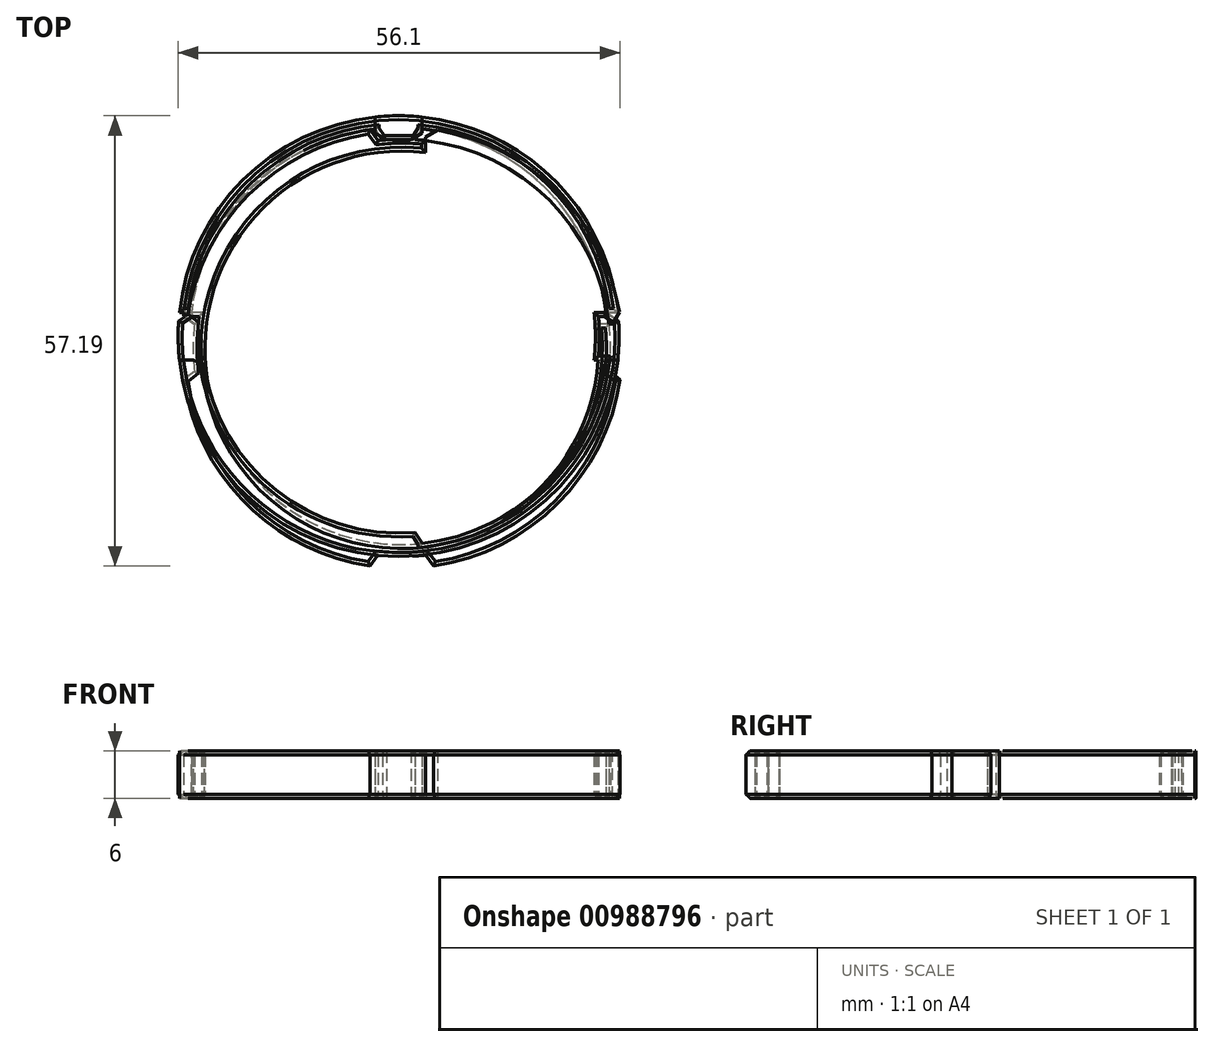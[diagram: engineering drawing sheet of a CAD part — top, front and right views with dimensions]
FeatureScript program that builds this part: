
annotation { "Feature Type Name" : "Feature", "Feature Type Description" : "" }
export const myFeature = defineFeature(function(context is Context, id is Id, definition is map)
    precondition{}
    {
        {
            var Q0;
            Q0=qCreatedBy(makeId("Top.planeOp"),FACE);
            var sketch = newSketch(context, id + "F0", { "sketchPlane" : qUnion([Q0])});
            skCircle(sketch, "E0", {"center": v(0, 0) * mm, "radius": 28 * mm});
            skCircle(sketch, "E1", {"center": v(0, 0) * mm, "radius": 25 * mm});
            skLineSegment(sketch, "E2.bottom", {"start": v(53.13, -3) * mm, "end": v(-53.13, -3) * mm});
            skLineSegment(sketch, "E2.top", {"start": v(53.13, 3) * mm, "end": v(-53.13, 3) * mm});
            skLineSegment(sketch, "E2.left", {"start": v(53.13, -3) * mm, "end": v(53.13, 3) * mm});
            skLineSegment(sketch, "E2.right", {"start": v(-53.13, -3) * mm, "end": v(-53.13, 3) * mm});
            skCircle(sketch, "E3", {"center": v(0, 0) * mm, "radius": 26.5 * mm});
            skLineSegment(sketch, "E4.bottom", {"start": v(3, -37.45) * mm, "end": v(-3, -37.45) * mm});
            skLineSegment(sketch, "E4.top", {"start": v(3, 37.45) * mm, "end": v(-3, 37.45) * mm});
            skLineSegment(sketch, "E4.left", {"start": v(3, -37.45) * mm, "end": v(3, 37.45) * mm});
            skLineSegment(sketch, "E4.right", {"start": v(-3, -37.45) * mm, "end": v(-3, 37.45) * mm});
            skSolve(sketch);
        }
        {
            var Q0;
            {var subQ0=sQuery(id+"F0.wireOp",EDGE,"E2.bottom");var subQ1=sQuery(id+"F0.wireOp",EDGE,"E1");var subQ2=makeQuery(id+"F0.imprint","INTERSECT",VERTEX,{"disambiguationData":[OD(0.0)],"derivedFrom":[subQ1,subQ0]});Q0=makeQuery(id+"F0.imprint","IMPRINT",FACE,{"disambiguationData":[TD([[makeQuery(id+"F0.imprint","IMPRINT",EDGE,{"disambiguationData":[TD([[subQ2,-1.0]])],"derivedFrom":subQ1}),-1.0]])]});}
            var Q1;
            {var subQ0=sQuery(id+"F0.wireOp",EDGE,"E2.top");var subQ1=sQuery(id+"F0.wireOp",EDGE,"E1");var subQ2=makeQuery(id+"F0.imprint","INTERSECT",VERTEX,{"disambiguationData":[OD(0.0)],"derivedFrom":[subQ1,subQ0]});Q1=makeQuery(id+"F0.imprint","IMPRINT",FACE,{"disambiguationData":[TD([[makeQuery(id+"F0.imprint","IMPRINT",EDGE,{"disambiguationData":[TD([[subQ2,1.0]])],"derivedFrom":subQ1}),-1.0]])]});}
            var Q2;
            {var subQ0=sQuery(id+"F0.wireOp",EDGE,"E2.bottom");var subQ1=sQuery(id+"F0.wireOp",EDGE,"E0");var subQ2=makeQuery(id+"F0.imprint","INTERSECT",VERTEX,{"disambiguationData":[OD(0.0)],"derivedFrom":[subQ1,subQ0]});Q2=makeQuery(id+"F0.imprint","IMPRINT",FACE,{"disambiguationData":[TD([[makeQuery(id+"F0.imprint","IMPRINT",EDGE,{"disambiguationData":[TD([[subQ2,-1.0]])],"derivedFrom":subQ1}),1.0]])]});}
            var Q3;
            {var subQ0=sQuery(id+"F0.wireOp",EDGE,"E2.top");var subQ1=sQuery(id+"F0.wireOp",EDGE,"E0");var subQ2=makeQuery(id+"F0.imprint","INTERSECT",VERTEX,{"disambiguationData":[OD(0.0)],"derivedFrom":[subQ1,subQ0]});Q3=makeQuery(id+"F0.imprint","IMPRINT",FACE,{"disambiguationData":[TD([[makeQuery(id+"F0.imprint","IMPRINT",EDGE,{"disambiguationData":[TD([[subQ2,-1.0]])],"derivedFrom":subQ1}),1.0]])]});}
            var Q4;
            {var subQ0=sQuery(id+"F0.wireOp",EDGE,"E2.top");var subQ1=sQuery(id+"F0.wireOp",EDGE,"E0");var subQ2=makeQuery(id+"F0.imprint","INTERSECT",VERTEX,{"disambiguationData":[OD(1.0)],"derivedFrom":[subQ1,subQ0]});Q4=makeQuery(id+"F0.imprint","IMPRINT",FACE,{"disambiguationData":[TD([[makeQuery(id+"F0.imprint","IMPRINT",EDGE,{"disambiguationData":[TD([[subQ2,1.0]])],"derivedFrom":subQ1}),1.0]])]});}
            var Q5;
            {var subQ0=sQuery(id+"F0.wireOp",EDGE,"E4.left");var subQ1=sQuery(id+"F0.wireOp",EDGE,"E0");var subQ2=makeQuery(id+"F0.imprint","INTERSECT",VERTEX,{"disambiguationData":[OD(0.0)],"derivedFrom":[subQ1,subQ0]});Q5=makeQuery(id+"F0.imprint","IMPRINT",FACE,{"disambiguationData":[TD([[makeQuery(id+"F0.imprint","IMPRINT",EDGE,{"disambiguationData":[TD([[subQ2,-1.0]])],"derivedFrom":subQ1}),1.0]])]});}
            var Q6;
            {var subQ0=sQuery(id+"F0.wireOp",EDGE,"E4.left");var subQ1=sQuery(id+"F0.wireOp",EDGE,"E1");var subQ2=makeQuery(id+"F0.imprint","INTERSECT",VERTEX,{"disambiguationData":[OD(0.0)],"derivedFrom":[subQ1,subQ0]});Q6=makeQuery(id+"F0.imprint","IMPRINT",FACE,{"disambiguationData":[TD([[makeQuery(id+"F0.imprint","IMPRINT",EDGE,{"disambiguationData":[TD([[subQ2,1.0]])],"derivedFrom":subQ1}),-1.0]])]});}
            var Q7;
            {var subQ0=sQuery(id+"F0.wireOp",EDGE,"E4.left");var subQ1=sQuery(id+"F0.wireOp",EDGE,"E1");var subQ2=makeQuery(id+"F0.imprint","INTERSECT",VERTEX,{"disambiguationData":[OD(1.0)],"derivedFrom":[subQ1,subQ0]});Q7=makeQuery(id+"F0.imprint","IMPRINT",FACE,{"disambiguationData":[TD([[makeQuery(id+"F0.imprint","IMPRINT",EDGE,{"disambiguationData":[TD([[subQ2,-1.0]])],"derivedFrom":subQ1}),-1.0]])]});}
            var Q8;
            {var subQ0=sQuery(id+"F0.wireOp",EDGE,"E4.right");var subQ1=sQuery(id+"F0.wireOp",EDGE,"E1");var subQ2=makeQuery(id+"F0.imprint","INTERSECT",VERTEX,{"disambiguationData":[OD(0.0)],"derivedFrom":[subQ1,subQ0]});Q8=makeQuery(id+"F0.imprint","IMPRINT",FACE,{"disambiguationData":[TD([[makeQuery(id+"F0.imprint","IMPRINT",EDGE,{"disambiguationData":[TD([[subQ2,-1.0]])],"derivedFrom":subQ1}),-1.0]])]});}
            var Q9;
            {var subQ0=sQuery(id+"F0.wireOp",EDGE,"E4.left");var subQ1=sQuery(id+"F0.wireOp",EDGE,"E0");var subQ2=makeQuery(id+"F0.imprint","INTERSECT",VERTEX,{"disambiguationData":[OD(1.0)],"derivedFrom":[subQ1,subQ0]});Q9=makeQuery(id+"F0.imprint","IMPRINT",FACE,{"disambiguationData":[TD([[makeQuery(id+"F0.imprint","IMPRINT",EDGE,{"disambiguationData":[TD([[subQ2,-1.0]])],"derivedFrom":subQ1}),1.0]])]});}
            var Q10;
            {var subQ0=sQuery(id+"F0.wireOp",EDGE,"E4.right");var subQ1=sQuery(id+"F0.wireOp",EDGE,"E0");var subQ2=makeQuery(id+"F0.imprint","INTERSECT",VERTEX,{"disambiguationData":[OD(1.0)],"derivedFrom":[subQ1,subQ0]});Q10=makeQuery(id+"F0.imprint","IMPRINT",FACE,{"disambiguationData":[TD([[makeQuery(id+"F0.imprint","IMPRINT",EDGE,{"disambiguationData":[TD([[subQ2,-1.0]])],"derivedFrom":subQ1}),1.0]])]});}
            var Q11;
            {var subQ0=sQuery(id+"F0.wireOp",EDGE,"E2.top");var subQ1=sQuery(id+"F0.wireOp",EDGE,"E1");var subQ2=makeQuery(id+"F0.imprint","INTERSECT",VERTEX,{"disambiguationData":[OD(1.0)],"derivedFrom":[subQ1,subQ0]});Q11=makeQuery(id+"F0.imprint","IMPRINT",FACE,{"disambiguationData":[TD([[makeQuery(id+"F0.imprint","IMPRINT",EDGE,{"disambiguationData":[TD([[subQ2,-1.0]])],"derivedFrom":subQ1}),-1.0]])]});}
            extrude(context, id + "F1", {"entities" : qUnion([Q0, Q1, Q2, Q3, Q4, Q5, Q6, Q7, Q8, Q9, Q10, Q11]), "depth" : 6 * mm, "offsetDistance" : 25 * mm});
        }
        {
            var Q0;
            {var subQ0=sQuery(id+"F0.wireOp",EDGE,"E4.right");var subQ1=sQuery(id+"F0.wireOp",EDGE,"E1");Q0=makeQuery(id+"F1.opExtrude","SWEPT_EDGE",EDGE,{"disambiguationData":[OSD([subQ1,subQ0]),TDD([makeQuery(id+"F0.imprint","INTERSECT",VERTEX,{"disambiguationData":[OD(0.0)],"derivedFrom":[subQ1,subQ0]})])]});}
            var Q1;
            {var subQ0=sQuery(id+"F0.wireOp",EDGE,"E4.left");var subQ1=sQuery(id+"F0.wireOp",EDGE,"E1");Q1=makeQuery(id+"F1.opExtrude","SWEPT_EDGE",EDGE,{"disambiguationData":[OSD([subQ1,subQ0]),TDD([makeQuery(id+"F0.imprint","INTERSECT",VERTEX,{"disambiguationData":[OD(1.0)],"derivedFrom":[subQ1,subQ0]})])]});}
            chamfer(context, id + "F2", {"entities" : qUnion([Q0, Q1]), "chamferType" : ChamferType.TWO_OFFSETS, "width1" : 1.5 * mm, "oppositeDirection" : false, "width2" : 1 * mm, "tangentPropagation" : true});
        }
        {
            var Q0;
            {var subQ0=sQuery(id+"F0.wireOp",EDGE,"E4.left");var subQ1=sQuery(id+"F0.wireOp",EDGE,"E1");Q0=makeQuery(id+"F1.opExtrude","SWEPT_EDGE",EDGE,{"disambiguationData":[OSD([subQ1,subQ0]),TDD([makeQuery(id+"F0.imprint","INTERSECT",VERTEX,{"disambiguationData":[OD(0.0)],"derivedFrom":[subQ1,subQ0]})])]});}
            var Q1;
            {var subQ0=sQuery(id+"F0.wireOp",EDGE,"E4.right");var subQ1=sQuery(id+"F0.wireOp",EDGE,"E1");Q1=makeQuery(id+"F1.opExtrude","SWEPT_EDGE",EDGE,{"disambiguationData":[OSD([subQ1,subQ0]),TDD([makeQuery(id+"F0.imprint","INTERSECT",VERTEX,{"disambiguationData":[OD(1.0)],"derivedFrom":[subQ1,subQ0]})])]});}
            chamfer(context, id + "F3", {"entities" : qUnion([Q0, Q1]), "chamferType" : ChamferType.TWO_OFFSETS, "width1" : 1 * mm, "oppositeDirection" : false, "width2" : 1.5 * mm, "tangentPropagation" : true});
        }
        {
            var Q0;
            {var subQ0=sQuery(id+"F0.wireOp",EDGE,"E2.bottom");var subQ1=sQuery(id+"F0.wireOp",EDGE,"E0");Q0=makeQuery(id+"F1.opExtrude","SWEPT_EDGE",EDGE,{"disambiguationData":[OSD([subQ1,subQ0]),TDD([makeQuery(id+"F0.imprint","INTERSECT",VERTEX,{"disambiguationData":[OD(1.0)],"derivedFrom":[subQ1,subQ0]})])]});}
            var Q1;
            {var subQ0=sQuery(id+"F0.wireOp",EDGE,"E2.top");var subQ1=sQuery(id+"F0.wireOp",EDGE,"E0");Q1=makeQuery(id+"F1.opExtrude","SWEPT_EDGE",EDGE,{"disambiguationData":[OSD([subQ1,subQ0]),TDD([makeQuery(id+"F0.imprint","INTERSECT",VERTEX,{"disambiguationData":[OD(1.0)],"derivedFrom":[subQ1,subQ0]})])]});}
            chamfer(context, id + "F4", {"entities" : qUnion([Q0, Q1]), "chamferType" : ChamferType.TWO_OFFSETS, "width1" : 1 * mm, "oppositeDirection" : true, "width2" : 1.5 * mm, "tangentPropagation" : true});
        }
        {
            var Q0;
            {var subQ0=sQuery(id+"F0.wireOp",EDGE,"E2.bottom");var subQ1=sQuery(id+"F0.wireOp",EDGE,"E0");Q0=makeQuery(id+"F1.opExtrude","SWEPT_EDGE",EDGE,{"disambiguationData":[OSD([subQ1,subQ0]),TDD([makeQuery(id+"F0.imprint","INTERSECT",VERTEX,{"disambiguationData":[OD(0.0)],"derivedFrom":[subQ1,subQ0]})])]});}
            var Q1;
            {var subQ0=sQuery(id+"F0.wireOp",EDGE,"E2.top");var subQ1=sQuery(id+"F0.wireOp",EDGE,"E0");Q1=makeQuery(id+"F1.opExtrude","SWEPT_EDGE",EDGE,{"disambiguationData":[OSD([subQ1,subQ0]),TDD([makeQuery(id+"F0.imprint","INTERSECT",VERTEX,{"disambiguationData":[OD(0.0)],"derivedFrom":[subQ1,subQ0]})])]});}
            chamfer(context, id + "F5", {"entities" : qUnion([Q0, Q1]), "chamferType" : ChamferType.TWO_OFFSETS, "width1" : 1 * mm, "oppositeDirection" : false, "width2" : 1.5 * mm, "tangentPropagation" : true});
        }
        {
            var Q0;
            Q0=makeQuery(id+"F1.opExtrude","CAP_FACE",FACE,{"disambiguationData":[OSD([sQuery(id+"F0.wireOp",EDGE,"E0"),sQuery(id+"F0.wireOp",EDGE,"E1"),sQuery(id+"F0.wireOp",EDGE,"E2.bottom"),sQuery(id+"F0.wireOp",EDGE,"E2.top"),sQuery(id+"F0.wireOp",EDGE,"E3"),sQuery(id+"F0.wireOp",EDGE,"E4.left"),sQuery(id+"F0.wireOp",EDGE,"E4.right")])],"isStart":false});
            var Q1;
            Q1=makeQuery(id+"F1.opExtrude","CAP_FACE",FACE,{"disambiguationData":[OSD([sQuery(id+"F0.wireOp",EDGE,"E0"),sQuery(id+"F0.wireOp",EDGE,"E1"),sQuery(id+"F0.wireOp",EDGE,"E2.bottom"),sQuery(id+"F0.wireOp",EDGE,"E2.top"),sQuery(id+"F0.wireOp",EDGE,"E3"),sQuery(id+"F0.wireOp",EDGE,"E4.left"),sQuery(id+"F0.wireOp",EDGE,"E4.right")])],"isStart":true});
            chamfer(context, id + "F6", {"entities" : qUnion([Q0, Q1]), "width" : 0.5 * mm, "tangentPropagation" : true});
        }
        {
            var Q0;
            Q0=qCreatedBy(makeId("Top.planeOp"),FACE);
            var sketch = newSketch(context, id + "F7", { "sketchPlane" : qUnion([Q0])});
            skCircle(sketch, "E5", {"center": v(0.4, -1.48) * mm, "radius": 28 * mm});
            skCircle(sketch, "E6", {"center": v(0.4, -1.48) * mm, "radius": 25 * mm});
            skLineSegment(sketch, "E7.bottom", {"start": v(53.53, -4.48) * mm, "end": v(-52.73, -4.48) * mm});
            skLineSegment(sketch, "E7.top", {"start": v(53.53, 1.52) * mm, "end": v(-52.73, 1.52) * mm});
            skLineSegment(sketch, "E7.left", {"start": v(53.53, -4.48) * mm, "end": v(53.53, 1.52) * mm});
            skLineSegment(sketch, "E7.right", {"start": v(-52.73, -4.48) * mm, "end": v(-52.73, 1.52) * mm});
            skCircle(sketch, "E8", {"center": v(0.4, -1.48) * mm, "radius": 26.5 * mm});
            skLineSegment(sketch, "E9.bottom", {"start": v(-2.6, -40.61) * mm, "end": v(3.4, -40.61) * mm});
            skLineSegment(sketch, "E9.top", {"start": v(-2.6, 37.65) * mm, "end": v(3.4, 37.65) * mm});
            skLineSegment(sketch, "E9.left", {"start": v(-2.6, -40.61) * mm, "end": v(-2.6, 37.65) * mm});
            skLineSegment(sketch, "E9.right", {"start": v(3.4, -40.61) * mm, "end": v(3.4, 37.65) * mm});
            skSolve(sketch);
        }
        {
            var Q0;
            {var subQ0=sQuery(id+"F7.wireOp",EDGE,"E9.right");var subQ1=sQuery(id+"F7.wireOp",EDGE,"E6");var subQ2=makeQuery(id+"F7.imprint","INTERSECT",VERTEX,{"disambiguationData":[OD(0.0)],"derivedFrom":[subQ1,subQ0]});Q0=makeQuery(id+"F7.imprint","IMPRINT",FACE,{"disambiguationData":[TD([[makeQuery(id+"F7.imprint","IMPRINT",EDGE,{"disambiguationData":[TD([[subQ2,-1.0]])],"derivedFrom":subQ1}),-1.0]])]});}
            var Q1;
            {var subQ0=sQuery(id+"F7.wireOp",EDGE,"E9.left");var subQ1=sQuery(id+"F7.wireOp",EDGE,"E6");var subQ2=makeQuery(id+"F7.imprint","INTERSECT",VERTEX,{"disambiguationData":[OD(0.0)],"derivedFrom":[subQ1,subQ0]});Q1=makeQuery(id+"F7.imprint","IMPRINT",FACE,{"disambiguationData":[TD([[makeQuery(id+"F7.imprint","IMPRINT",EDGE,{"disambiguationData":[TD([[subQ2,-1.0]])],"derivedFrom":subQ1}),-1.0]])]});}
            var Q2;
            {var subQ0=sQuery(id+"F7.wireOp",EDGE,"E9.left");var subQ1=sQuery(id+"F7.wireOp",EDGE,"E5");var subQ2=makeQuery(id+"F7.imprint","INTERSECT",VERTEX,{"disambiguationData":[OD(0.0)],"derivedFrom":[subQ1,subQ0]});Q2=makeQuery(id+"F7.imprint","IMPRINT",FACE,{"disambiguationData":[TD([[makeQuery(id+"F7.imprint","IMPRINT",EDGE,{"disambiguationData":[TD([[subQ2,-1.0]])],"derivedFrom":subQ1}),1.0]])]});}
            var Q3;
            {var subQ0=sQuery(id+"F7.wireOp",EDGE,"E9.right");var subQ1=sQuery(id+"F7.wireOp",EDGE,"E6");var subQ2=makeQuery(id+"F7.imprint","INTERSECT",VERTEX,{"disambiguationData":[OD(0.0)],"derivedFrom":[subQ1,subQ0]});Q3=makeQuery(id+"F7.imprint","IMPRINT",FACE,{"disambiguationData":[TD([[makeQuery(id+"F7.imprint","IMPRINT",EDGE,{"disambiguationData":[TD([[subQ2,1.0]])],"derivedFrom":subQ1}),-1.0]])]});}
            var Q4;
            {var subQ0=sQuery(id+"F7.wireOp",EDGE,"E9.right");var subQ1=sQuery(id+"F7.wireOp",EDGE,"E5");var subQ2=makeQuery(id+"F7.imprint","INTERSECT",VERTEX,{"disambiguationData":[OD(0.0)],"derivedFrom":[subQ1,subQ0]});Q4=makeQuery(id+"F7.imprint","IMPRINT",FACE,{"disambiguationData":[TD([[makeQuery(id+"F7.imprint","IMPRINT",EDGE,{"disambiguationData":[TD([[subQ2,1.0]])],"derivedFrom":subQ1}),1.0]])]});}
            var Q5;
            {var subQ0=sQuery(id+"F7.wireOp",EDGE,"E7.top");var subQ1=sQuery(id+"F7.wireOp",EDGE,"E6");var subQ2=makeQuery(id+"F7.imprint","INTERSECT",VERTEX,{"disambiguationData":[OD(1.0)],"derivedFrom":[subQ1,subQ0]});Q5=makeQuery(id+"F7.imprint","IMPRINT",FACE,{"disambiguationData":[TD([[makeQuery(id+"F7.imprint","IMPRINT",EDGE,{"disambiguationData":[TD([[subQ2,-1.0]])],"derivedFrom":subQ1}),-1.0]])]});}
            var Q6;
            {var subQ0=sQuery(id+"F7.wireOp",EDGE,"E7.bottom");var subQ1=sQuery(id+"F7.wireOp",EDGE,"E6");var subQ2=makeQuery(id+"F7.imprint","INTERSECT",VERTEX,{"disambiguationData":[OD(0.0)],"derivedFrom":[subQ1,subQ0]});Q6=makeQuery(id+"F7.imprint","IMPRINT",FACE,{"disambiguationData":[TD([[makeQuery(id+"F7.imprint","IMPRINT",EDGE,{"disambiguationData":[TD([[subQ2,-1.0]])],"derivedFrom":subQ1}),-1.0]])]});}
            var Q7;
            {var subQ0=sQuery(id+"F7.wireOp",EDGE,"E7.bottom");var subQ1=sQuery(id+"F7.wireOp",EDGE,"E5");var subQ2=makeQuery(id+"F7.imprint","INTERSECT",VERTEX,{"disambiguationData":[OD(0.0)],"derivedFrom":[subQ1,subQ0]});Q7=makeQuery(id+"F7.imprint","IMPRINT",FACE,{"disambiguationData":[TD([[makeQuery(id+"F7.imprint","IMPRINT",EDGE,{"disambiguationData":[TD([[subQ2,-1.0]])],"derivedFrom":subQ1}),1.0]])]});}
            var Q8;
            {var subQ0=sQuery(id+"F7.wireOp",EDGE,"E9.left");var subQ1=sQuery(id+"F7.wireOp",EDGE,"E6");var subQ2=makeQuery(id+"F7.imprint","INTERSECT",VERTEX,{"disambiguationData":[OD(1.0)],"derivedFrom":[subQ1,subQ0]});Q8=makeQuery(id+"F7.imprint","IMPRINT",FACE,{"disambiguationData":[TD([[makeQuery(id+"F7.imprint","IMPRINT",EDGE,{"disambiguationData":[TD([[subQ2,-1.0]])],"derivedFrom":subQ1}),-1.0]])]});}
            var Q9;
            {var subQ0=sQuery(id+"F7.wireOp",EDGE,"E9.right");var subQ1=sQuery(id+"F7.wireOp",EDGE,"E6");var subQ2=makeQuery(id+"F7.imprint","INTERSECT",VERTEX,{"disambiguationData":[OD(1.0)],"derivedFrom":[subQ1,subQ0]});Q9=makeQuery(id+"F7.imprint","IMPRINT",FACE,{"disambiguationData":[TD([[makeQuery(id+"F7.imprint","IMPRINT",EDGE,{"disambiguationData":[TD([[subQ2,-1.0]])],"derivedFrom":subQ1}),-1.0]])]});}
            var Q10;
            {var subQ0=sQuery(id+"F7.wireOp",EDGE,"E9.right");var subQ1=sQuery(id+"F7.wireOp",EDGE,"E5");var subQ2=makeQuery(id+"F7.imprint","INTERSECT",VERTEX,{"disambiguationData":[OD(1.0)],"derivedFrom":[subQ1,subQ0]});Q10=makeQuery(id+"F7.imprint","IMPRINT",FACE,{"disambiguationData":[TD([[makeQuery(id+"F7.imprint","IMPRINT",EDGE,{"disambiguationData":[TD([[subQ2,-1.0]])],"derivedFrom":subQ1}),1.0]])]});}
            var Q11;
            {var subQ0=sQuery(id+"F7.wireOp",EDGE,"E7.top");var subQ1=sQuery(id+"F7.wireOp",EDGE,"E6");var subQ2=makeQuery(id+"F7.imprint","INTERSECT",VERTEX,{"disambiguationData":[OD(0.0)],"derivedFrom":[subQ1,subQ0]});Q11=makeQuery(id+"F7.imprint","IMPRINT",FACE,{"disambiguationData":[TD([[makeQuery(id+"F7.imprint","IMPRINT",EDGE,{"disambiguationData":[TD([[subQ2,1.0]])],"derivedFrom":subQ1}),-1.0]])]});}
            extrude(context, id + "F8", {"entities" : qUnion([Q0, Q1, Q2, Q3, Q4, Q5, Q6, Q7, Q8, Q9, Q10, Q11]), "depth" : 6 * mm, "offsetDistance" : 25 * mm});
        }
        {
            var Q0;
            {var subQ0=sQuery(id+"F7.wireOp",EDGE,"E7.top");var subQ1=sQuery(id+"F7.wireOp",EDGE,"E5");Q0=makeQuery(id+"F8.opExtrude","SWEPT_EDGE",EDGE,{"disambiguationData":[OSD([subQ1,subQ0]),TDD([makeQuery(id+"F7.imprint","INTERSECT",VERTEX,{"disambiguationData":[OD(1.0)],"derivedFrom":[subQ1,subQ0]})])]});}
            var Q1;
            {var subQ0=sQuery(id+"F7.wireOp",EDGE,"E9.left");var subQ1=sQuery(id+"F7.wireOp",EDGE,"E5");Q1=makeQuery(id+"F8.opExtrude","SWEPT_EDGE",EDGE,{"disambiguationData":[OSD([subQ1,subQ0]),TDD([makeQuery(id+"F7.imprint","INTERSECT",VERTEX,{"disambiguationData":[OD(1.0)],"derivedFrom":[subQ1,subQ0]})])]});}
            var Q2;
            {var subQ0=sQuery(id+"F7.wireOp",EDGE,"E7.bottom");var subQ1=sQuery(id+"F7.wireOp",EDGE,"E5");Q2=makeQuery(id+"F8.opExtrude","SWEPT_EDGE",EDGE,{"disambiguationData":[OSD([subQ1,subQ0]),TDD([makeQuery(id+"F7.imprint","INTERSECT",VERTEX,{"disambiguationData":[OD(1.0)],"derivedFrom":[subQ1,subQ0]})])]});}
            var Q3;
            {var subQ0=sQuery(id+"F7.wireOp",EDGE,"E9.right");var subQ1=sQuery(id+"F7.wireOp",EDGE,"E5");Q3=makeQuery(id+"F8.opExtrude","SWEPT_EDGE",EDGE,{"disambiguationData":[OSD([subQ1,subQ0]),TDD([makeQuery(id+"F7.imprint","INTERSECT",VERTEX,{"disambiguationData":[OD(0.0)],"derivedFrom":[subQ1,subQ0]})])]});}
            chamfer(context, id + "F9", {"entities" : qUnion([Q0, Q1, Q2, Q3]), "chamferType" : ChamferType.TWO_OFFSETS, "width1" : 1 * mm, "oppositeDirection" : true, "width2" : 1.5 * mm, "tangentPropagation" : true});
        }
        {
            var Q0;
            {var subQ0=sQuery(id+"F7.wireOp",EDGE,"E9.left");var subQ1=sQuery(id+"F7.wireOp",EDGE,"E5");Q0=makeQuery(id+"F8.opExtrude","SWEPT_EDGE",EDGE,{"disambiguationData":[OSD([subQ1,subQ0]),TDD([makeQuery(id+"F7.imprint","INTERSECT",VERTEX,{"disambiguationData":[OD(0.0)],"derivedFrom":[subQ1,subQ0]})])]});}
            var Q1;
            {var subQ0=sQuery(id+"F7.wireOp",EDGE,"E7.bottom");var subQ1=sQuery(id+"F7.wireOp",EDGE,"E5");Q1=makeQuery(id+"F8.opExtrude","SWEPT_EDGE",EDGE,{"disambiguationData":[OSD([subQ1,subQ0]),TDD([makeQuery(id+"F7.imprint","INTERSECT",VERTEX,{"disambiguationData":[OD(0.0)],"derivedFrom":[subQ1,subQ0]})])]});}
            var Q2;
            {var subQ0=sQuery(id+"F7.wireOp",EDGE,"E9.right");var subQ1=sQuery(id+"F7.wireOp",EDGE,"E5");Q2=makeQuery(id+"F8.opExtrude","SWEPT_EDGE",EDGE,{"disambiguationData":[OSD([subQ1,subQ0]),TDD([makeQuery(id+"F7.imprint","INTERSECT",VERTEX,{"disambiguationData":[OD(1.0)],"derivedFrom":[subQ1,subQ0]})])]});}
            var Q3;
            {var subQ0=sQuery(id+"F7.wireOp",EDGE,"E7.top");var subQ1=sQuery(id+"F7.wireOp",EDGE,"E5");Q3=makeQuery(id+"F8.opExtrude","SWEPT_EDGE",EDGE,{"disambiguationData":[OSD([subQ1,subQ0]),TDD([makeQuery(id+"F7.imprint","INTERSECT",VERTEX,{"disambiguationData":[OD(0.0)],"derivedFrom":[subQ1,subQ0]})])]});}
            chamfer(context, id + "F10", {"entities" : qUnion([Q0, Q1, Q2, Q3]), "chamferType" : ChamferType.TWO_OFFSETS, "width1" : 1 * mm, "oppositeDirection" : false, "width2" : 1.5 * mm, "tangentPropagation" : true});
        }
        {
            var Q0;
            Q0=makeQuery(id+"F8.opExtrude","CAP_FACE",FACE,{"disambiguationData":[OSD([sQuery(id+"F7.wireOp",EDGE,"E5"),sQuery(id+"F7.wireOp",EDGE,"E6"),sQuery(id+"F7.wireOp",EDGE,"E7.bottom"),sQuery(id+"F7.wireOp",EDGE,"E7.top"),sQuery(id+"F7.wireOp",EDGE,"E8"),sQuery(id+"F7.wireOp",EDGE,"E9.left"),sQuery(id+"F7.wireOp",EDGE,"E9.right")])],"isStart":true});
            var Q1;
            Q1=makeQuery(id+"F8.opExtrude","CAP_FACE",FACE,{"disambiguationData":[OSD([sQuery(id+"F7.wireOp",EDGE,"E5"),sQuery(id+"F7.wireOp",EDGE,"E6"),sQuery(id+"F7.wireOp",EDGE,"E7.bottom"),sQuery(id+"F7.wireOp",EDGE,"E7.top"),sQuery(id+"F7.wireOp",EDGE,"E8"),sQuery(id+"F7.wireOp",EDGE,"E9.left"),sQuery(id+"F7.wireOp",EDGE,"E9.right")])],"isStart":false});
            chamfer(context, id + "F11", {"entities" : qUnion([Q0, Q1]), "width" : 0.5 * mm, "tangentPropagation" : true});
        }
        {
            var Q0;
            Q0=qCreatedBy(makeId("Top.planeOp"),FACE);
            var sketch = newSketch(context, id + "F12", { "sketchPlane" : qUnion([Q0])});
            skCircle(sketch, "E10", {"center": v(0, 0) * mm, "radius": 28 * mm});
            skCircle(sketch, "E11", {"center": v(0, 0) * mm, "radius": 25 * mm});
            skLineSegment(sketch, "E12.bottom", {"start": v(53.13, -3) * mm, "end": v(-53.13, -3) * mm});
            skLineSegment(sketch, "E12.top", {"start": v(53.13, 3) * mm, "end": v(-53.13, 3) * mm});
            skLineSegment(sketch, "E12.left", {"start": v(53.13, -3) * mm, "end": v(53.13, 3) * mm});
            skLineSegment(sketch, "E12.right", {"start": v(-53.13, -3) * mm, "end": v(-53.13, 3) * mm});
            skCircle(sketch, "E13", {"center": v(0, 0) * mm, "radius": 26.5 * mm});
            skLineSegment(sketch, "E14.bottom", {"start": v(3, -47.17) * mm, "end": v(-3, -47.17) * mm});
            skLineSegment(sketch, "E14.top", {"start": v(3, 47.17) * mm, "end": v(-3, 47.17) * mm});
            skLineSegment(sketch, "E14.left", {"start": v(3, -47.17) * mm, "end": v(3, 47.17) * mm});
            skLineSegment(sketch, "E14.right", {"start": v(-3, -47.17) * mm, "end": v(-3, 47.17) * mm});
            skSolve(sketch);
        }
        {
            var Q0;
            {var subQ0=sQuery(id+"F12.wireOp",EDGE,"E14.left");var subQ1=sQuery(id+"F12.wireOp",EDGE,"E10");var subQ2=makeQuery(id+"F12.imprint","INTERSECT",VERTEX,{"disambiguationData":[OD(0.0)],"derivedFrom":[subQ1,subQ0]});Q0=makeQuery(id+"F12.imprint","IMPRINT",FACE,{"disambiguationData":[TD([[makeQuery(id+"F12.imprint","IMPRINT",EDGE,{"disambiguationData":[TD([[subQ2,1.0]])],"derivedFrom":subQ1}),1.0]])]});}
            var Q1;
            {var subQ0=sQuery(id+"F12.wireOp",EDGE,"E14.right");var subQ1=sQuery(id+"F12.wireOp",EDGE,"E10");var subQ2=makeQuery(id+"F12.imprint","INTERSECT",VERTEX,{"disambiguationData":[OD(0.0)],"derivedFrom":[subQ1,subQ0]});Q1=makeQuery(id+"F12.imprint","IMPRINT",FACE,{"disambiguationData":[TD([[makeQuery(id+"F12.imprint","IMPRINT",EDGE,{"disambiguationData":[TD([[subQ2,-1.0]])],"derivedFrom":subQ1}),1.0]])]});}
            var Q2;
            {var subQ0=sQuery(id+"F12.wireOp",EDGE,"E12.bottom");var subQ1=sQuery(id+"F12.wireOp",EDGE,"E10");var subQ2=makeQuery(id+"F12.imprint","INTERSECT",VERTEX,{"disambiguationData":[OD(0.0)],"derivedFrom":[subQ1,subQ0]});Q2=makeQuery(id+"F12.imprint","IMPRINT",FACE,{"disambiguationData":[TD([[makeQuery(id+"F12.imprint","IMPRINT",EDGE,{"disambiguationData":[TD([[subQ2,-1.0]])],"derivedFrom":subQ1}),1.0]])]});}
            var Q3;
            {var subQ0=sQuery(id+"F12.wireOp",EDGE,"E14.left");var subQ1=sQuery(id+"F12.wireOp",EDGE,"E10");var subQ2=makeQuery(id+"F12.imprint","INTERSECT",VERTEX,{"disambiguationData":[OD(1.0)],"derivedFrom":[subQ1,subQ0]});Q3=makeQuery(id+"F12.imprint","IMPRINT",FACE,{"disambiguationData":[TD([[makeQuery(id+"F12.imprint","IMPRINT",EDGE,{"disambiguationData":[TD([[subQ2,-1.0]])],"derivedFrom":subQ1}),1.0]])]});}
            var Q4;
            {var subQ0=sQuery(id+"F12.wireOp",EDGE,"E14.left");var subQ1=sQuery(id+"F12.wireOp",EDGE,"E10");var subQ2=makeQuery(id+"F12.imprint","INTERSECT",VERTEX,{"disambiguationData":[OD(0.0)],"derivedFrom":[subQ1,subQ0]});Q4=makeQuery(id+"F12.imprint","IMPRINT",FACE,{"disambiguationData":[TD([[makeQuery(id+"F12.imprint","IMPRINT",EDGE,{"disambiguationData":[TD([[subQ2,-1.0]])],"derivedFrom":subQ1}),1.0]])]});}
            var Q5;
            {var subQ0=sQuery(id+"F12.wireOp",EDGE,"E12.top");var subQ1=sQuery(id+"F12.wireOp",EDGE,"E10");var subQ2=makeQuery(id+"F12.imprint","INTERSECT",VERTEX,{"disambiguationData":[OD(1.0)],"derivedFrom":[subQ1,subQ0]});Q5=makeQuery(id+"F12.imprint","IMPRINT",FACE,{"disambiguationData":[TD([[makeQuery(id+"F12.imprint","IMPRINT",EDGE,{"disambiguationData":[TD([[subQ2,-1.0]])],"derivedFrom":subQ1}),1.0]])]});}
            var Q6;
            {var subQ0=sQuery(id+"F12.wireOp",EDGE,"E14.right");var subQ1=sQuery(id+"F12.wireOp",EDGE,"E10");var subQ2=makeQuery(id+"F12.imprint","INTERSECT",VERTEX,{"disambiguationData":[OD(1.0)],"derivedFrom":[subQ1,subQ0]});Q6=makeQuery(id+"F12.imprint","IMPRINT",FACE,{"disambiguationData":[TD([[makeQuery(id+"F12.imprint","IMPRINT",EDGE,{"disambiguationData":[TD([[subQ2,-1.0]])],"derivedFrom":subQ1}),1.0]])]});}
            var Q7;
            {var subQ0=sQuery(id+"F12.wireOp",EDGE,"E12.top");var subQ1=sQuery(id+"F12.wireOp",EDGE,"E10");var subQ2=makeQuery(id+"F12.imprint","INTERSECT",VERTEX,{"disambiguationData":[OD(0.0)],"derivedFrom":[subQ1,subQ0]});Q7=makeQuery(id+"F12.imprint","IMPRINT",FACE,{"disambiguationData":[TD([[makeQuery(id+"F12.imprint","IMPRINT",EDGE,{"disambiguationData":[TD([[subQ2,1.0]])],"derivedFrom":subQ1}),1.0]])]});}
            var Q8;
            {var subQ0=sQuery(id+"F12.wireOp",EDGE,"E12.bottom");var subQ1=sQuery(id+"F12.wireOp",EDGE,"E11");var subQ2=makeQuery(id+"F12.imprint","INTERSECT",VERTEX,{"disambiguationData":[OD(0.0)],"derivedFrom":[subQ1,subQ0]});Q8=makeQuery(id+"F12.imprint","IMPRINT",FACE,{"disambiguationData":[TD([[makeQuery(id+"F12.imprint","IMPRINT",EDGE,{"disambiguationData":[TD([[subQ2,-1.0]])],"derivedFrom":subQ1}),-1.0]])]});}
            var Q9;
            {var subQ0=sQuery(id+"F12.wireOp",EDGE,"E14.left");var subQ1=sQuery(id+"F12.wireOp",EDGE,"E11");var subQ2=makeQuery(id+"F12.imprint","INTERSECT",VERTEX,{"disambiguationData":[OD(1.0)],"derivedFrom":[subQ1,subQ0]});Q9=makeQuery(id+"F12.imprint","IMPRINT",FACE,{"disambiguationData":[TD([[makeQuery(id+"F12.imprint","IMPRINT",EDGE,{"disambiguationData":[TD([[subQ2,-1.0]])],"derivedFrom":subQ1}),-1.0]])]});}
            var Q10;
            {var subQ0=sQuery(id+"F12.wireOp",EDGE,"E14.left");var subQ1=sQuery(id+"F12.wireOp",EDGE,"E11");var subQ2=makeQuery(id+"F12.imprint","INTERSECT",VERTEX,{"disambiguationData":[OD(0.0)],"derivedFrom":[subQ1,subQ0]});Q10=makeQuery(id+"F12.imprint","IMPRINT",FACE,{"disambiguationData":[TD([[makeQuery(id+"F12.imprint","IMPRINT",EDGE,{"disambiguationData":[TD([[subQ2,1.0]])],"derivedFrom":subQ1}),-1.0]])]});}
            var Q11;
            {var subQ0=sQuery(id+"F12.wireOp",EDGE,"E14.right");var subQ1=sQuery(id+"F12.wireOp",EDGE,"E11");var subQ2=makeQuery(id+"F12.imprint","INTERSECT",VERTEX,{"disambiguationData":[OD(0.0)],"derivedFrom":[subQ1,subQ0]});Q11=makeQuery(id+"F12.imprint","IMPRINT",FACE,{"disambiguationData":[TD([[makeQuery(id+"F12.imprint","IMPRINT",EDGE,{"disambiguationData":[TD([[subQ2,-1.0]])],"derivedFrom":subQ1}),-1.0]])]});}
            extrude(context, id + "F13", {"entities" : qUnion([Q0, Q1, Q2, Q3, Q4, Q5, Q6, Q7, Q8, Q9, Q10, Q11]), "depth" : 6 * mm, "offsetDistance" : 25 * mm});
        }
        {
            var Q0;
            {var subQ0=sQuery(id+"F12.wireOp",EDGE,"E12.top");var subQ1=sQuery(id+"F12.wireOp",EDGE,"E11");Q0=makeQuery(id+"F13.opExtrude","SWEPT_EDGE",EDGE,{"disambiguationData":[OSD([subQ1,subQ0]),TDD([makeQuery(id+"F12.imprint","INTERSECT",VERTEX,{"disambiguationData":[OD(1.0)],"derivedFrom":[subQ1,subQ0]})])]});}
            var Q1;
            {var subQ0=sQuery(id+"F12.wireOp",EDGE,"E14.left");var subQ1=sQuery(id+"F12.wireOp",EDGE,"E11");Q1=makeQuery(id+"F13.opExtrude","SWEPT_EDGE",EDGE,{"disambiguationData":[OSD([subQ1,subQ0]),TDD([makeQuery(id+"F12.imprint","INTERSECT",VERTEX,{"disambiguationData":[OD(0.0)],"derivedFrom":[subQ1,subQ0]})])]});}
            var Q2;
            {var subQ0=sQuery(id+"F12.wireOp",EDGE,"E14.right");var subQ1=sQuery(id+"F12.wireOp",EDGE,"E11");Q2=makeQuery(id+"F13.opExtrude","SWEPT_EDGE",EDGE,{"disambiguationData":[OSD([subQ1,subQ0]),TDD([makeQuery(id+"F12.imprint","INTERSECT",VERTEX,{"disambiguationData":[OD(1.0)],"derivedFrom":[subQ1,subQ0]})])]});}
            var Q3;
            {var subQ0=sQuery(id+"F12.wireOp",EDGE,"E12.bottom");var subQ1=sQuery(id+"F12.wireOp",EDGE,"E11");Q3=makeQuery(id+"F13.opExtrude","SWEPT_EDGE",EDGE,{"disambiguationData":[OSD([subQ1,subQ0]),TDD([makeQuery(id+"F12.imprint","INTERSECT",VERTEX,{"disambiguationData":[OD(1.0)],"derivedFrom":[subQ1,subQ0]})])]});}
            chamfer(context, id + "F14", {"entities" : qUnion([Q0, Q1, Q2, Q3]), "chamferType" : ChamferType.TWO_OFFSETS, "width1" : 1 * mm, "oppositeDirection" : false, "width2" : 1.5 * mm, "tangentPropagation" : true});
        }
        {
            var Q0;
            {var subQ0=sQuery(id+"F12.wireOp",EDGE,"E12.bottom");var subQ1=sQuery(id+"F12.wireOp",EDGE,"E11");Q0=makeQuery(id+"F13.opExtrude","SWEPT_EDGE",EDGE,{"disambiguationData":[OSD([subQ1,subQ0]),TDD([makeQuery(id+"F12.imprint","INTERSECT",VERTEX,{"disambiguationData":[OD(0.0)],"derivedFrom":[subQ1,subQ0]})])]});}
            var Q1;
            {var subQ0=sQuery(id+"F12.wireOp",EDGE,"E14.left");var subQ1=sQuery(id+"F12.wireOp",EDGE,"E11");Q1=makeQuery(id+"F13.opExtrude","SWEPT_EDGE",EDGE,{"disambiguationData":[OSD([subQ1,subQ0]),TDD([makeQuery(id+"F12.imprint","INTERSECT",VERTEX,{"disambiguationData":[OD(1.0)],"derivedFrom":[subQ1,subQ0]})])]});}
            var Q2;
            {var subQ0=sQuery(id+"F12.wireOp",EDGE,"E14.right");var subQ1=sQuery(id+"F12.wireOp",EDGE,"E11");Q2=makeQuery(id+"F13.opExtrude","SWEPT_EDGE",EDGE,{"disambiguationData":[OSD([subQ1,subQ0]),TDD([makeQuery(id+"F12.imprint","INTERSECT",VERTEX,{"disambiguationData":[OD(0.0)],"derivedFrom":[subQ1,subQ0]})])]});}
            var Q3;
            {var subQ0=sQuery(id+"F12.wireOp",EDGE,"E12.top");var subQ1=sQuery(id+"F12.wireOp",EDGE,"E11");Q3=makeQuery(id+"F13.opExtrude","SWEPT_EDGE",EDGE,{"disambiguationData":[OSD([subQ1,subQ0]),TDD([makeQuery(id+"F12.imprint","INTERSECT",VERTEX,{"disambiguationData":[OD(0.0)],"derivedFrom":[subQ1,subQ0]})])]});}
            chamfer(context, id + "F15", {"entities" : qUnion([Q0, Q1, Q2, Q3]), "chamferType" : ChamferType.TWO_OFFSETS, "width1" : 1.5 * mm, "oppositeDirection" : false, "width2" : 1 * mm, "tangentPropagation" : true});
        }
        {
            var Q0;
            Q0=makeQuery(id+"F13.opExtrude","CAP_FACE",FACE,{"disambiguationData":[OSD([sQuery(id+"F12.wireOp",EDGE,"E10"),sQuery(id+"F12.wireOp",EDGE,"E11"),sQuery(id+"F12.wireOp",EDGE,"E12.bottom"),sQuery(id+"F12.wireOp",EDGE,"E12.top"),sQuery(id+"F12.wireOp",EDGE,"E13"),sQuery(id+"F12.wireOp",EDGE,"E14.left"),sQuery(id+"F12.wireOp",EDGE,"E14.right")])],"isStart":false});
            var Q1;
            Q1=makeQuery(id+"F13.opExtrude","CAP_FACE",FACE,{"disambiguationData":[OSD([sQuery(id+"F12.wireOp",EDGE,"E10"),sQuery(id+"F12.wireOp",EDGE,"E11"),sQuery(id+"F12.wireOp",EDGE,"E12.bottom"),sQuery(id+"F12.wireOp",EDGE,"E12.top"),sQuery(id+"F12.wireOp",EDGE,"E13"),sQuery(id+"F12.wireOp",EDGE,"E14.left"),sQuery(id+"F12.wireOp",EDGE,"E14.right")])],"isStart":true});
            chamfer(context, id + "F16", {"entities" : qUnion([Q0, Q1]), "width" : 0.5 * mm, "tangentPropagation" : true});
        }
    });
